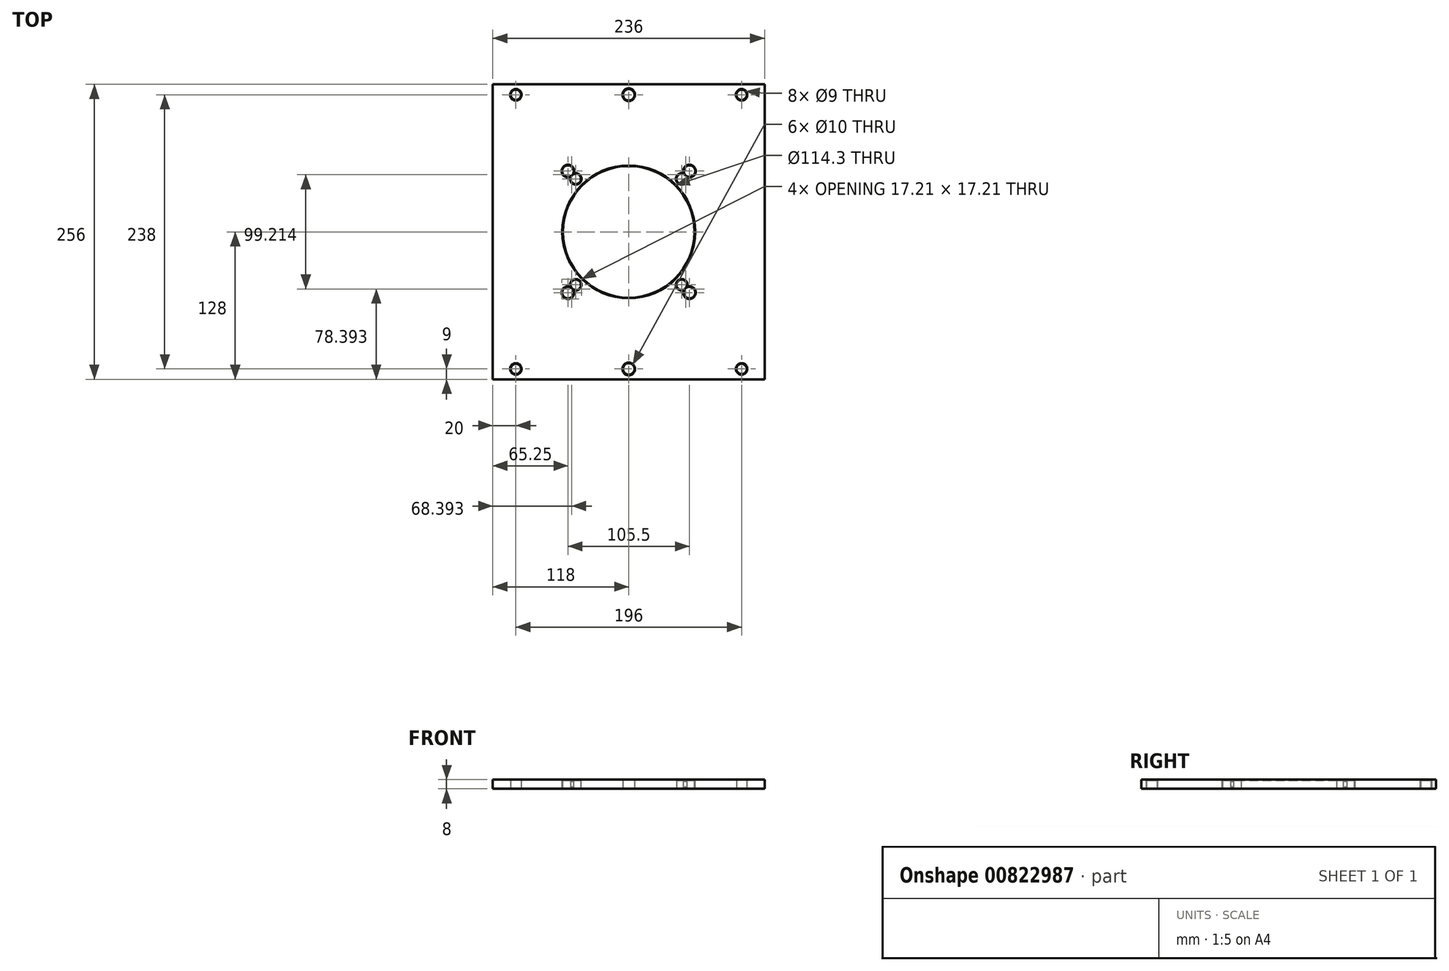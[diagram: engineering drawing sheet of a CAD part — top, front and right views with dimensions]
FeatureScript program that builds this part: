
annotation { "Feature Type Name" : "Feature", "Feature Type Description" : "" }
export const myFeature = defineFeature(function(context is Context, id is Id, definition is map)
    precondition{}
    {
        {
            var Q0;
            Q0=qCreatedBy(makeId("Top.planeOp"),FACE);
            var sketch = newSketch(context, id + "F0", { "sketchPlane" : qUnion([Q0])});
            skLineSegment(sketch, "E0.bottom", {"start": v(-118, -128) * mm, "end": v(118, -128) * mm});
            skLineSegment(sketch, "E0.top", {"start": v(-118, 128) * mm, "end": v(118, 128) * mm});
            skLineSegment(sketch, "E0.left", {"start": v(-118, -128) * mm, "end": v(-118, 128) * mm});
            skLineSegment(sketch, "E0.right", {"start": v(118, -128) * mm, "end": v(118, 128) * mm});
            skCircle(sketch, "E1", {"center": v(0, 0) * mm, "radius": 55 * mm});
            skCircle(sketch, "E2", {"center": v(0, 0) * mm, "radius": 65 * mm, "construction": true});
            skLineSegment(sketch, "E3", {"start": v(0, 0) * mm, "end": v(118, 0) * mm, "construction": true});
            skLineSegment(sketch, "E4", {"start": v(118, 0) * mm, "end": v(0, 128) * mm, "construction": true});
            skLineSegment(sketch, "E5", {"start": v(0, 128) * mm, "end": v(0, 0) * mm, "construction": true});
            skCircle(sketch, "E6", {"center": v(45.96, 45.96) * mm, "radius": 4.5 * mm});
            skLineSegment(sketch, "E7", {"start": v(0, 0) * mm, "end": v(45.96, 45.96) * mm, "construction": true});
            skCircle(sketch, "E8.MirrorC", {"center": v(-45.96, 45.96) * mm, "radius": 4.5 * mm});
            skCircle(sketch, "E9.MirrorC", {"center": v(45.96, -45.96) * mm, "radius": 4.5 * mm});
            skCircle(sketch, "E10.MirrorC", {"center": v(-45.96, -45.96) * mm, "radius": 4.5 * mm});
            skCircle(sketch, "E11", {"center": v(0, 0) * mm, "radius": 100 * mm, "construction": true});
            skLineSegment(sketch, "E12.0", {"start": v(-118, 119) * mm, "end": v(118, 119) * mm, "construction": true});
            skLineSegment(sketch, "E13.0", {"start": v(-118, -119) * mm, "end": v(118, -119) * mm, "construction": true});
            skCircle(sketch, "E14", {"center": v(98, 119) * mm, "radius": 4.5 * mm});
            skCircle(sketch, "E15.MirrorC", {"center": v(-98, 119) * mm, "radius": 4.5 * mm});
            skCircle(sketch, "E16.MirrorC", {"center": v(-98, -119) * mm, "radius": 4.5 * mm});
            skCircle(sketch, "E17.MirrorC", {"center": v(98, -119) * mm, "radius": 4.5 * mm});
            skCircle(sketch, "E18", {"center": v(0, 119) * mm, "radius": 5 * mm});
            skCircle(sketch, "E19.MirrorC", {"center": v(0, -119) * mm, "radius": 5 * mm});
            skSolve(sketch);
        }
        {
            var Q0;
            Q0=qSketchRegion(id+"F0",true);
            extrude(context, id + "F1", {"entities" : qUnion([Q0]), "depth" : 8 * mm, "offsetDistance" : 25 * mm});
        }
        {
            var Q0;
            Q0=makeQuery(id+"F1.opExtrude","SWEPT_FACE",FACE,{"disambiguationData":[OSD([sQuery(id+"F0.wireOp",EDGE,"E16.MirrorC")])]});
            var Q1;
            Q1=makeQuery(id+"F1.opExtrude","SWEPT_FACE",FACE,{"disambiguationData":[OSD([sQuery(id+"F0.wireOp",EDGE,"E10.MirrorC")])]});
            var Q2;
            Q2=makeQuery(id+"F1.opExtrude","SWEPT_FACE",FACE,{"disambiguationData":[OSD([sQuery(id+"F0.wireOp",EDGE,"E1")])]});
            var Q3;
            Q3=makeQuery(id+"F1.opExtrude","SWEPT_FACE",FACE,{"disambiguationData":[OSD([sQuery(id+"F0.wireOp",EDGE,"E8.MirrorC")])]});
            var Q4;
            Q4=makeQuery(id+"F1.opExtrude","SWEPT_FACE",FACE,{"disambiguationData":[OSD([sQuery(id+"F0.wireOp",EDGE,"E9.MirrorC")])]});
            var Q5;
            Q5=makeQuery(id+"F1.opExtrude","SWEPT_FACE",FACE,{"disambiguationData":[OSD([sQuery(id+"F0.wireOp",EDGE,"E17.MirrorC")])]});
            var Q6;
            Q6=makeQuery(id+"F1.opExtrude","SWEPT_FACE",FACE,{"disambiguationData":[OSD([sQuery(id+"F0.wireOp",EDGE,"E15.MirrorC")])]});
            var Q7;
            Q7=makeQuery(id+"F1.opExtrude","SWEPT_FACE",FACE,{"disambiguationData":[OSD([sQuery(id+"F0.wireOp",EDGE,"E6")])]});
            var Q8;
            Q8=makeQuery(id+"F1.opExtrude","SWEPT_FACE",FACE,{"disambiguationData":[OSD([sQuery(id+"F0.wireOp",EDGE,"E14")])]});
            var Q9;
            Q9=makeQuery(id+"F1.opExtrude","SWEPT_FACE",FACE,{"disambiguationData":[OSD([sQuery(id+"F0.wireOp",EDGE,"E18")])]});
            var Q10;
            Q10=makeQuery(id+"F1.opExtrude","SWEPT_FACE",FACE,{"disambiguationData":[OSD([sQuery(id+"F0.wireOp",EDGE,"E19.MirrorC")])]});
            chamfer(context, id + "F2", {"entities" : qUnion([Q0, Q1, Q2, Q3, Q4, Q5, Q6, Q7, Q8, Q9, Q10]), "width" : 0.5 * mm, "tangentPropagation" : true});
        }
        {
            var Q0;
            Q0=makeQuery(id+"F1.opExtrude","CAP_FACE",FACE,{"disambiguationData":[OSD([sQuery(id+"F0.wireOp",EDGE,"E0.bottom"),sQuery(id+"F0.wireOp",EDGE,"E0.top"),sQuery(id+"F0.wireOp",EDGE,"E0.left"),sQuery(id+"F0.wireOp",EDGE,"E0.right"),sQuery(id+"F0.wireOp",EDGE,"E1"),sQuery(id+"F0.wireOp",EDGE,"E6"),sQuery(id+"F0.wireOp",EDGE,"E8.MirrorC"),sQuery(id+"F0.wireOp",EDGE,"E9.MirrorC"),sQuery(id+"F0.wireOp",EDGE,"E10.MirrorC"),sQuery(id+"F0.wireOp",EDGE,"E14"),sQuery(id+"F0.wireOp",EDGE,"E15.MirrorC"),sQuery(id+"F0.wireOp",EDGE,"E16.MirrorC"),sQuery(id+"F0.wireOp",EDGE,"E17.MirrorC"),sQuery(id+"F0.wireOp",EDGE,"E18"),sQuery(id+"F0.wireOp",EDGE,"E19.MirrorC")])],"isStart":false});
            var sketch = newSketch(context, id + "F3", { "sketchPlane" : qUnion([Q0])});
            skCircle(sketch, "E20", {"center": v(0, 0) * mm, "radius": 57.15 * mm});
            skCircle(sketch, "E21", {"center": v(0, 0) * mm, "radius": 74.6 * mm, "construction": true});
            skCircle(sketch, "E22", {"center": v(52.75, 52.75) * mm, "radius": 5 * mm});
            skLineSegment(sketch, "E23", {"start": v(52.75, 52.75) * mm, "end": v(0, 0) * mm, "construction": true});
            skLineSegment(sketch, "E24", {"start": v(0, 0) * mm, "end": v(90.37, 0) * mm, "construction": true});
            skCircle(sketch, "E25.1.0", {"center": v(-52.75, 52.75) * mm, "radius": 5 * mm});
            skCircle(sketch, "E25.2.0", {"center": v(-52.75, -52.75) * mm, "radius": 5 * mm});
            skCircle(sketch, "E25.3.0", {"center": v(52.75, -52.75) * mm, "radius": 5 * mm});
            skSolve(sketch);
        }
        {
            var Q0;
            Q0 = qSketchRegion(id + "F3", true);
            extrude(context, id + "F4", {"entities" : qUnion([Q0]), "operationType" : NewBodyOperationType.REMOVE, "oppositeDirection" : true, "depth" : 25 * mm, "offsetDistance" : 25 * mm});
        }
        {
            var Q0;
            Q0=makeQuery(id+"F4.boolean.opBoolean","COPY",FACE,{"derivedFrom":makeQuery(id+"F4.opExtrude","SWEPT_FACE",FACE,{"disambiguationData":[OSD([sQuery(id+"F3.wireOp",EDGE,"E25.2.0")])]})});
            var Q1;
            Q1=makeQuery(id+"F4.boolean.opBoolean","COPY",FACE,{"derivedFrom":makeQuery(id+"F4.opExtrude","SWEPT_FACE",FACE,{"disambiguationData":[OSD([sQuery(id+"F3.wireOp",EDGE,"E25.3.0")])]})});
            var Q2;
            Q2=makeQuery(id+"F4.boolean.opBoolean","COPY",FACE,{"derivedFrom":makeQuery(id+"F4.opExtrude","SWEPT_FACE",FACE,{"disambiguationData":[OSD([sQuery(id+"F3.wireOp",EDGE,"E22")])]})});
            var Q3;
            Q3=makeQuery(id+"F4.boolean.opBoolean","COPY",FACE,{"derivedFrom":makeQuery(id+"F4.opExtrude","SWEPT_FACE",FACE,{"disambiguationData":[OSD([sQuery(id+"F3.wireOp",EDGE,"E25.1.0")])]})});
            var Q4;
            Q4=makeQuery(id+"F4.boolean.opBoolean","COPY",FACE,{"derivedFrom":makeQuery(id+"F4.opExtrude","SWEPT_FACE",FACE,{"disambiguationData":[OSD([sQuery(id+"F3.wireOp",EDGE,"E20")])]})});
            chamfer(context, id + "F5", {"entities" : qUnion([Q0, Q1, Q2, Q3, Q4]), "width" : 0.5 * mm, "tangentPropagation" : true});
        }
    });
